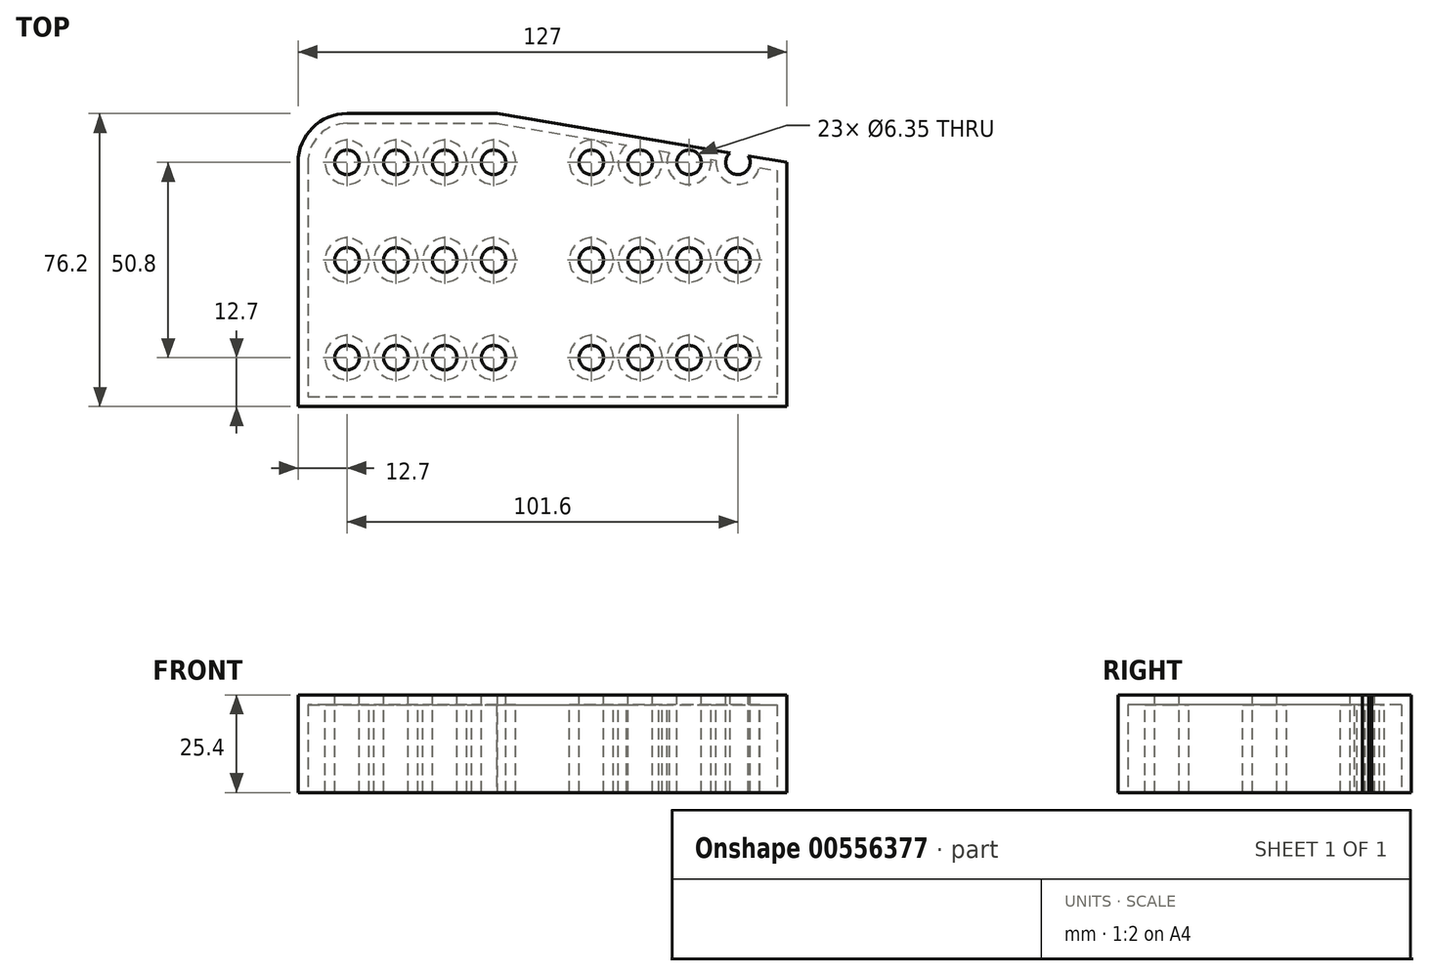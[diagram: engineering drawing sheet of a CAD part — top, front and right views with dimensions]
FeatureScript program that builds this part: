
annotation { "Feature Type Name" : "Feature", "Feature Type Description" : "" }
export const myFeature = defineFeature(function(context is Context, id is Id, definition is map)
    precondition{}
    {
        {
            var Q0;
            Q0=qCreatedBy(makeId("Top.planeOp"),FACE);
            var sketch = newSketch(context, id + "F0", { "sketchPlane" : qUnion([Q0])});
            skLineSegment(sketch, "E0.bottom", {"start": v(12.7, 0) * mm, "end": v(51.72, 0) * mm});
            skLineSegment(sketch, "E0.top", {"start": v(0, -76.2) * mm, "end": v(127, -76.2) * mm});
            skLineSegment(sketch, "E0.left", {"start": v(0, -12.7) * mm, "end": v(0, -76.2) * mm});
            skLineSegment(sketch, "E0.right", {"start": v(127, -12.7) * mm, "end": v(127, -76.2) * mm});
            skPoint(sketch, "E1.visualSharp", {"position": v(0, 0) * mm});
            skArc(sketch, "E1.filletArc", {"start": v(12.7, 0) * mm, "mid": v(3.72, -3.72) * mm, "end": v(0, -12.7) * mm});
            skLineSegment(sketch, "E2", {"start": v(51.72, 0) * mm, "end": v(127, -12.7) * mm});
            skSolve(sketch);
        }
        {
            var Q0;
            Q0 = qSketchRegion(id + "F0", true);
            extrude(context, id + "F1", {"entities" : qUnion([Q0]), "depth" : 25.4 * mm, "offsetDistance" : 25.4 * mm});
        }
        {
            var Q0;
            Q0=makeQuery(id+"F1.opExtrude","CAP_FACE",FACE,{"disambiguationData":[OSD([sQuery(id+"F0.wireOp",EDGE,"E0.bottom"),sQuery(id+"F0.wireOp",EDGE,"E0.top"),sQuery(id+"F0.wireOp",EDGE,"E0.left"),sQuery(id+"F0.wireOp",EDGE,"E0.right"),sQuery(id+"F0.wireOp",EDGE,"E1.filletArc"),sQuery(id+"F0.wireOp",EDGE,"E2")])],"isStart":false});
            var sketch = newSketch(context, id + "F2", { "sketchPlane" : qUnion([Q0])});
            skCircle(sketch, "E3", {"center": v(12.7, -12.7) * mm, "radius": 3.18 * mm});
            skCircle(sketch, "E4.0.1.0", {"center": v(12.7, -38.1) * mm, "radius": 3.18 * mm});
            skCircle(sketch, "E4.0.2.0", {"center": v(12.7, -63.5) * mm, "radius": 3.18 * mm});
            skCircle(sketch, "E4.1.0.0", {"center": v(25.4, -12.7) * mm, "radius": 3.18 * mm});
            skCircle(sketch, "E4.1.1.0", {"center": v(25.4, -38.1) * mm, "radius": 3.18 * mm});
            skCircle(sketch, "E4.1.2.0", {"center": v(25.4, -63.5) * mm, "radius": 3.18 * mm});
            skCircle(sketch, "E4.2.0.0", {"center": v(38.1, -12.7) * mm, "radius": 3.18 * mm});
            skCircle(sketch, "E4.2.1.0", {"center": v(38.1, -38.1) * mm, "radius": 3.18 * mm});
            skCircle(sketch, "E4.2.2.0", {"center": v(38.1, -63.5) * mm, "radius": 3.18 * mm});
            skCircle(sketch, "E4.3.0.0", {"center": v(50.8, -12.7) * mm, "radius": 3.18 * mm});
            skCircle(sketch, "E4.3.1.0", {"center": v(50.8, -38.1) * mm, "radius": 3.18 * mm});
            skCircle(sketch, "E4.3.2.0", {"center": v(50.8, -63.5) * mm, "radius": 3.18 * mm});
            skLineSegment(sketch, "E4.direction1", {"start": v(12.7, -12.7) * mm, "end": v(25.4, -12.7) * mm, "construction": true});
            skLineSegment(sketch, "E4.direction2", {"start": v(12.7, -12.7) * mm, "end": v(12.7, -38.1) * mm, "construction": true});
            skLineSegment(sketch, "E5", {"start": v(63.5, -76.2) * mm, "end": v(63.5, 0) * mm, "construction": true});
            skCircle(sketch, "E6.MirrorC", {"center": v(114.3, -12.7) * mm, "radius": 3.18 * mm});
            skCircle(sketch, "E7.MirrorC", {"center": v(101.6, -12.7) * mm, "radius": 3.18 * mm});
            skCircle(sketch, "E8.MirrorC", {"center": v(88.9, -12.7) * mm, "radius": 3.18 * mm});
            skCircle(sketch, "E9.MirrorC", {"center": v(114.3, -38.1) * mm, "radius": 3.18 * mm});
            skCircle(sketch, "E10.MirrorC", {"center": v(101.6, -38.1) * mm, "radius": 3.18 * mm});
            skCircle(sketch, "E11.MirrorC", {"center": v(88.9, -38.1) * mm, "radius": 3.18 * mm});
            skCircle(sketch, "E12.MirrorC", {"center": v(114.3, -63.5) * mm, "radius": 3.18 * mm});
            skCircle(sketch, "E13.MirrorC", {"center": v(101.6, -63.5) * mm, "radius": 3.18 * mm});
            skCircle(sketch, "E14.MirrorC", {"center": v(88.9, -63.5) * mm, "radius": 3.18 * mm});
            skCircle(sketch, "E15.MirrorC", {"center": v(76.2, -63.5) * mm, "radius": 3.18 * mm});
            skCircle(sketch, "E16.MirrorC", {"center": v(76.2, -38.1) * mm, "radius": 3.18 * mm});
            skCircle(sketch, "E17.MirrorC", {"center": v(76.2, -12.7) * mm, "radius": 3.18 * mm});
            skSolve(sketch);
        }
        {
            var Q0;
            Q0 = qSketchRegion(id + "F2", true);
            extrude(context, id + "F3", {"entities" : qUnion([Q0]), "operationType" : NewBodyOperationType.REMOVE, "oppositeDirection" : true, "depth" : 25.4 * mm, "offsetDistance" : 25.4 * mm});
        }
        {
            var Q0;
            Q0=makeQuery(id+"F1.opExtrude","CAP_FACE",FACE,{"disambiguationData":[OSD([sQuery(id+"F0.wireOp",EDGE,"E0.bottom"),sQuery(id+"F0.wireOp",EDGE,"E0.top"),sQuery(id+"F0.wireOp",EDGE,"E0.left"),sQuery(id+"F0.wireOp",EDGE,"E0.right"),sQuery(id+"F0.wireOp",EDGE,"E1.filletArc"),sQuery(id+"F0.wireOp",EDGE,"E2")])],"isStart":true});
            shell(context, id + "F4", {"entities" : qUnion([Q0]), "thickness" : 2.54 * mm});
        }
    });
